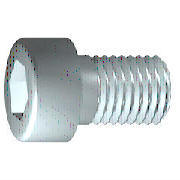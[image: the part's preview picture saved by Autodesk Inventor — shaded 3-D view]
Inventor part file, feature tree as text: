
AUTODESK INVENTOR PART (.ipt)
format: ipt  version: 2023.3 (Build 273359000, 359)  size: 190,464 bytes
history: native  units: mm (DEFAULTED — no unit token found)
features: sketch x2, other x1, extrude x1, plane x1, fillet x1
ambient origin geometry x7: Origin, YZ Plane, XY Plane, X Axis, Y Axis, Z Axis, Center Point
bodies: Solid1 (feature_tree)
feature tree (6):
  other  "Körper"
  extrude  "Loch"  Depth=2.5mm
  plane  "Work Plane1"
  fillet  "Fillet2"  Radius=2.5mm
  sketch  "Skizze1"  dims[d1=10.875mm d2=0.276153mm d3=2.5mm]
  sketch  "Skizze2"  dims[d4=1.1mm d5=60.0deg d6=2.5mm d7=2.5mm d8=2.309401mm d9=4.5mm d10=90.0deg d11=10.0mm d12=0.0mm d13=10.875mm d14=0.0mm d15=0.276052mm d16=0.276053mm d17=0.25mm d19=0.0mm d26=12.0mm d27=45.0deg d28=0.0mm d29=0.0mm d30=0.1mm]
